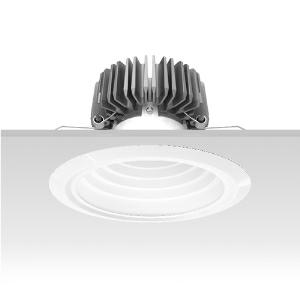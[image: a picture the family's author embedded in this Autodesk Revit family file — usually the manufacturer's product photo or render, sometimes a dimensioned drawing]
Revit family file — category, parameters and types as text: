
# Revit family: 3f_filippi_-_3f_reno_bianco_ampio_3f_filippi_-_30629_a01025_-_3f_reno_200_wh_3000-840_wide___vt_wh_c12f
name_source: partatom
category: Lighting Fixtures
units: mm (PartAtom-declared; Revit-internal decimal feet)

## family parameters
Cut with Voids When Loaded = No
Host = Face
Light Source = No
Part Type = Normal
Room Calculation Point = No
Round Connector Dimension = Use Diameter
Shared = No

## types (1)
- 3F Filippi - 3F Reno Bianco Ampio (1 x LED, 2529 lm, 28 W, 4000 K)
    Apparent Load = 28 VA
    Approval mark = CE
    CIE Flux Codes = 75 94 99 100 100
    Color Rendering = 80
    Color Temperature = 4000 K
    Control Gear = Electronic ballast
    Default Elevation = 1800 mm
    Description = ILLUMINOTECHNICAL
Luminous efficiency 100% (DLOR 100%, ULOR 0%).
Initial luminous flux of the luminaire 2529 lm.
Direct symmetric wide distribution.
Installation Interdistance Transv.D = 1.56 x hu - Long.D = 1.56 x hu.
Tabular UGR (CIE 117 - 4H-8H; S=0.25H; 70/50/20): RUG 21.8 - 21.7.
Beam angle: 74° - 74°.
Luminous efficacy 90 lm/W.
Lifetime (L90/B10): 30000 h. (tq+25°C)
Lifetime (L85/B10): 50000 h. (tq+25°C)
Lifetime (L70/B10): 80000 h. (tq+25°C)
Sudden decreased luminous flux after 50000 hours: 0% (C0).
Photobiological safety in compliance with IEC/TR 62778: RG0 risk exempt, (IEC 62471).
In compliance with IEC/EN 62722-2-1 - IEC/EN 62717 standards.

SOURCE
Compact LED module 3000/840.
Energy efficiency class (UE 2019/2020 - UE 2019/2015): D.
CIE 13.3 Colour rendering index: CRI >80 (R9 <50%).
IES TM-30 Fidelity Index: Rf = 84 Rg = 95.
CCT nominal colour temperature 4000 K.
Colour initial tolerance (MacAdam): SDCM 3.
Zhaga Book 3 compliant.

MECHANICAL
Passive heat dissipator in die-casting aluminium, oversized, for optimum thermal management of the LED module.
Parabolic element with graduated/concentric rings in white polycarbonate.
Transparent external lens with glossy and satin differentiated surfaces, with a cooling and anti-insect system in methacrylate (PMMA).
Fastening spring clips in stainless steel.
Dimensions: diameter 226 mm, height 146 mm. Weight 1.69 kg.
IP44 protection degree for exposed part, IP20 for recessed part.
Mechanical strength to impacts IK06 (1 joule).
Glow-wire test resistance 650°C.

ELECTRICAL
Wiring on a separate unit.
Halogen Free electronic wiring 230V-50/60Hz, power factor 0.95, THD <25%, constant output current, SELV, class II, 1 driver.
Power of the luminaire 28 W.
ENEC - CE.
SAFE FLICKER: PstLM=<1 and SVM=<0.4 (IEC TR 61547-1 and IEC TR 63158), to ensure a more comfortable and safe light.
Luminaire compliant with EN 60598-2-22 for power supply from a centralised emergency system CPSS (Central Power Supply System), not incorporated in the luminaire - high risk areas excluded. The default power and flux are 100% in AC and 100% in DC.
Ambient temperature from 0°C to +25°C.
Temperature class T6 max 85°C.
Relative humidity UR: <85%.

INSTALLATION
Pull-up recessed fitting.
False ceiling carving: 200 mm.
All accessories dedicated to this product are available on the Catalog and on our website www.3F-Filippi.com.

ACCESSORIES
A01025 - VT transparent glass, tempered, not flammable, locked and in line with the trim, in white polycarbonate.

APPLICATIONS
Environments: architectural, commercial, exhibition areas, transit areas, corridors, shops, display windows, service areas.
In false ceilings with narrow voids.

WARNING
Luminaire designed for disposal/recycling at end-of-life.
Replaceable (LED only) light source by a professional. Replaceable control gear by a professional.
    Height = 0 mm  [stored 0 ft]
    Lamp = 1 x LED
    Lamp Light Flux = 2529 lm
    Lamp Power = 28 W
    Lamp count = 1
    Length = 226 mm
    Lifetime = 50000 h
    Luminous efficacy = 90 lm/W
    Manufacturer = 3F Filippi
    ModVariant = No
    Model = 3F Filippi - 30629+A01025 - 3F Reno 200 WH 3000-840 WIDE + VT WH
    Mounting Place = Ceiling
    Mounting Type = Recessed
    Number of Poles = 1
    OnlyDefault = Yes
    Power Factor = 1
    Product Name = 3F Filippi - 3F Reno Bianco Ampio
    Product group = recessed luminaire
    ProductGroupID = 4
    Protection Class = Protection class II
    Protection Degree = IP 20
    RLX_Detail_Level = 1
    RLX_Emergency_Light_Flux = 0 lm
    RLX_Emergency_Type = 0
    RLX_Emergency_Type_DB = No
    RlxData = <blob elided: 95781 chars, md5=aaa46873>
    Socket = socket
    Standby Power = 0 W
    System Light Flux = 2529 lm
    System Power = 28 W
    Type Comments = Product without accessories
    Type Image = 3ffilippi_3f_reno_200_wh__a01025.jpg
    URL = http://relux.com
    VarID = ---
    Voltage = 0 V
    Weight = 0.00 kg
    Width = 0 mm  [stored 0 ft]

note: [stored X ft] marks values corroborated as IEEE doubles in the binary element streams (Revit-internal decimal feet)

## geometry (parser evidence)
native form markers: Blend x4, Sweep x11
no freeform markers — native parametric forms only
